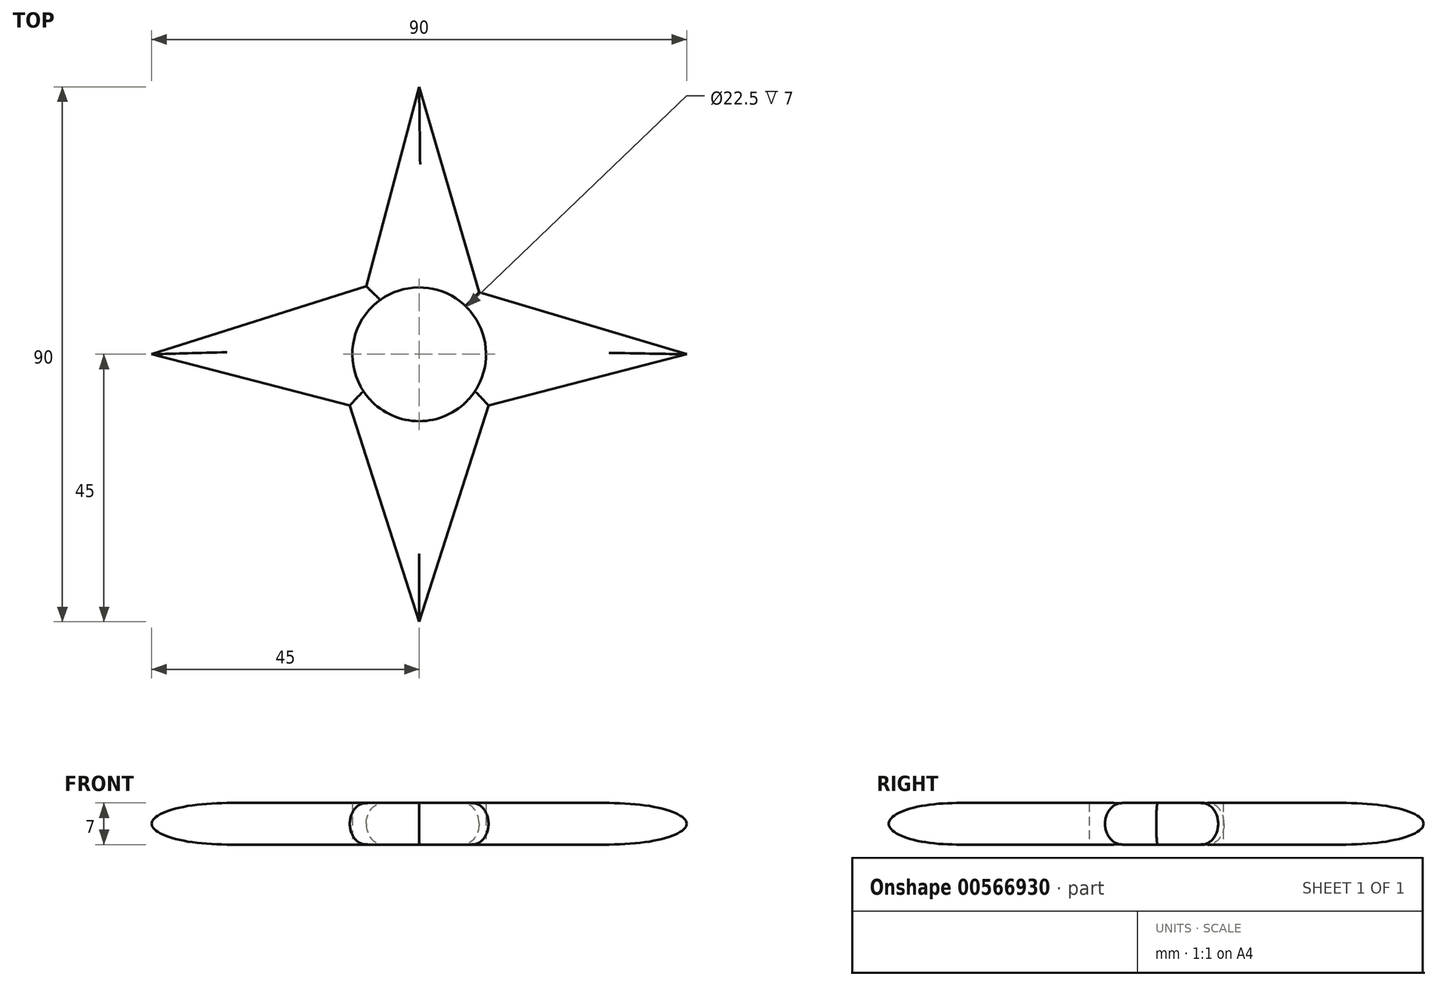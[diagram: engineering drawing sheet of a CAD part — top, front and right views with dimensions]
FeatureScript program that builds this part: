
annotation { "Feature Type Name" : "Feature", "Feature Type Description" : "" }
export const myFeature = defineFeature(function(context is Context, id is Id, definition is map)
    precondition{}
    {
        {
            var Q0;
            Q0=qCreatedBy(makeId("Top.planeOp"),FACE);
            var sketch = newSketch(context, id + "F0", { "sketchPlane" : qUnion([Q0])});
            skCircle(sketch, "E0", {"center": v(0, 0) * mm, "radius": 11.25 * mm});
            skCircle(sketch, "E1", {"center": v(0, 0) * mm, "radius": 14.5 * mm});
            skLineSegment(sketch, "E2", {"start": v(10.08, 10.43) * mm, "end": v(45, 0) * mm});
            skLineSegment(sketch, "E3", {"start": v(45, 0) * mm, "end": v(11.67, -8.6) * mm});
            skLineSegment(sketch, "E4", {"start": v(-11.67, -8.6) * mm, "end": v(-45, 0) * mm});
            skLineSegment(sketch, "E5", {"start": v(-45, 0) * mm, "end": v(-8.92, 11.43) * mm});
            skLineSegment(sketch, "E6", {"start": v(-8.92, 11.43) * mm, "end": v(0, 45) * mm});
            skLineSegment(sketch, "E7", {"start": v(0, 45) * mm, "end": v(10.08, 10.43) * mm});
            skLineSegment(sketch, "E8", {"start": v(-11.67, -8.6) * mm, "end": v(0, -45) * mm});
            skLineSegment(sketch, "E9", {"start": v(0, -45) * mm, "end": v(11.67, -8.6) * mm});
            skSolve(sketch);
        }
        {
            var Q0;
            Q0=qSketchRegion(id+"F0",true);
            extrude(context, id + "F1", {"entities" : qUnion([Q0]), "depth" : 7 * mm});
        }
        {
            var Q0;
            Q0=makeQuery(id+"F1.opExtrude","CAP_EDGE",EDGE,{"disambiguationData":[OSD([sQuery(id+"F0.wireOp",EDGE,"E7")])],"isStart":false});
            var Q1;
            Q1=makeQuery(id+"F1.opExtrude","CAP_EDGE",EDGE,{"disambiguationData":[OSD([sQuery(id+"F0.wireOp",EDGE,"E6")])],"isStart":false});
            var Q2;
            Q2=makeQuery(id+"F1.opExtrude","CAP_EDGE",EDGE,{"disambiguationData":[OSD([sQuery(id+"F0.wireOp",EDGE,"E5")])],"isStart":false});
            var Q3;
            Q3=makeQuery(id+"F1.opExtrude","CAP_EDGE",EDGE,{"disambiguationData":[OSD([sQuery(id+"F0.wireOp",EDGE,"E4")])],"isStart":false});
            var Q4;
            Q4=makeQuery(id+"F1.opExtrude","CAP_EDGE",EDGE,{"disambiguationData":[OSD([sQuery(id+"F0.wireOp",EDGE,"E8")])],"isStart":false});
            var Q5;
            Q5=makeQuery(id+"F1.opExtrude","CAP_EDGE",EDGE,{"disambiguationData":[OSD([sQuery(id+"F0.wireOp",EDGE,"E9")])],"isStart":false});
            var Q6;
            Q6=makeQuery(id+"F1.opExtrude","CAP_EDGE",EDGE,{"disambiguationData":[OSD([sQuery(id+"F0.wireOp",EDGE,"E3")])],"isStart":false});
            var Q7;
            Q7=makeQuery(id+"F1.opExtrude","CAP_EDGE",EDGE,{"disambiguationData":[OSD([sQuery(id+"F0.wireOp",EDGE,"E2")])],"isStart":false});
            fillet(context, id + "F2", {"entities" : qUnion([Q0, Q1, Q2, Q3, Q4, Q5, Q6, Q7]), "radius" : 3.5 * mm, "tangentPropagation" : true, "allowEdgeOverflow" : false});
        }
        {
            var Q0;
            Q0=makeQuery(id+"F1.opExtrude","CAP_EDGE",EDGE,{"disambiguationData":[OSD([sQuery(id+"F0.wireOp",EDGE,"E7")])],"isStart":true});
            var Q1;
            Q1=makeQuery(id+"F1.opExtrude","CAP_EDGE",EDGE,{"disambiguationData":[OSD([sQuery(id+"F0.wireOp",EDGE,"E2")])],"isStart":true});
            var Q2;
            Q2=makeQuery(id+"F1.opExtrude","CAP_EDGE",EDGE,{"disambiguationData":[OSD([sQuery(id+"F0.wireOp",EDGE,"E3")])],"isStart":true});
            var Q3;
            Q3=makeQuery(id+"F1.opExtrude","CAP_EDGE",EDGE,{"disambiguationData":[OSD([sQuery(id+"F0.wireOp",EDGE,"E9")])],"isStart":true});
            var Q4;
            Q4=makeQuery(id+"F1.opExtrude","CAP_EDGE",EDGE,{"disambiguationData":[OSD([sQuery(id+"F0.wireOp",EDGE,"E8")])],"isStart":true});
            var Q5;
            Q5=makeQuery(id+"F1.opExtrude","CAP_EDGE",EDGE,{"disambiguationData":[OSD([sQuery(id+"F0.wireOp",EDGE,"E4")])],"isStart":true});
            var Q6;
            Q6=makeQuery(id+"F1.opExtrude","CAP_EDGE",EDGE,{"disambiguationData":[OSD([sQuery(id+"F0.wireOp",EDGE,"E5")])],"isStart":true});
            var Q7;
            Q7=makeQuery(id+"F1.opExtrude","CAP_EDGE",EDGE,{"disambiguationData":[OSD([sQuery(id+"F0.wireOp",EDGE,"E6")])],"isStart":true});
            fillet(context, id + "F3", {"entities" : qUnion([Q0, Q1, Q2, Q3, Q4, Q5, Q6, Q7]), "radius" : 3.5 * mm, "tangentPropagation" : true, "allowEdgeOverflow" : false});
        }
    });
